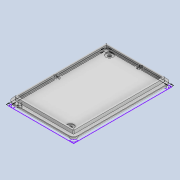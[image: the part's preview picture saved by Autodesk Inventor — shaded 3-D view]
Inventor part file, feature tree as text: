
AUTODESK INVENTOR PART (.ipt)
format: ipt  version: 2020 (Build 240168000, 168)  size: 237,056 bytes
history: native  units: mm
features: sketch x5, extrude x5, fillet x2, chamfer x1
ambient origin geometry x8: Origin, YZ Plane, XZ Plane, XY Plane, X Axis, Y Axis, Z Axis, Center Point
bodies: Body1 (feature_tree)
feature tree (13):
  sketch  "Sketch1"  dims[d0=50.0mm d1=75.0mm d2=45.0mm]
  extrude  "Extrusion3"  Depth=75.0mm
  fillet  "Fillet1"  Radius=45.0mm
  sketch  "Sketch2"  dims[d3=70.0mm d8=2.5mm d9=2.5mm]
  extrude  "Extrusion11"  Depth=2.5mm
  fillet  "Fillet2"  Radius=2.5mm
  extrude  "Extrusion12"  Depth=3.0mm
  extrude  "Extrusion13"  Depth=1.5mm
  extrude  "Extrusion14"  Depth=0.5mm
  chamfer  "Chamfer2"  Distance=1.5mm
  sketch  "Sketch4"  dims[d24=3.5mm d25=0.0mm d28=3.0mm]
  sketch  "Sketch6"  dims[d29=1.5mm d30=1.5mm]
  sketch  "Sketch7"  dims[d31=2.75mm d32=5.5mm d33=1.5mm d34=1.5mm d35=2.75mm d36=45.0deg d37=5.5mm d38=20.0mm d40=360.0deg d43=20.0mm d44=1.2mm d45=1.2mm d60=2.5mm d61=2.5mm d68=1.0mm d69=1.0mm d70=1.0mm d71=1.0mm d72=1.0mm d73=3.0mm d74=0.0mm d75=0.5mm d76=0.5mm d77=0.0mm d78=5.0mm d79=0.0mm d80=5.0mm d81=0.0mm d82=0.5mm d83=2.0mm d84=45.0deg]
